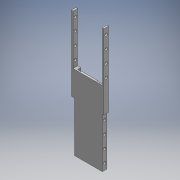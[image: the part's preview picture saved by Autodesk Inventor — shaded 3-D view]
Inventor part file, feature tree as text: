
AUTODESK INVENTOR PART (.ipt)
format: ipt  version: 2016 (Build 200138000, 138)  size: 206,336 bytes
history: native  units: mm
features: sketch x5, extrude x3, hole x2
ambient origin geometry x8: Origin, YZ Plane, XZ Plane, XY Plane, X Axis, Y Axis, Z Axis, Center Point
bodies: Solid1 (feature_tree)
feature tree (10):
  extrude  "Extrusion1"  Depth=80.0mm
  extrude  "Extrusion3"  Depth=2.5mm
  extrude  "Extrusion4"  Depth=44.5mm
  hole  "Hole1"  [1 undecoded]
  hole  "Hole2"  [1 undecoded]
  sketch  "Sketch1"  dims[d0=2.5mm d1=80.0mm]
  sketch  "Sketch4"  dims[d2=47.0mm d3=2.5mm]
  sketch  "Sketch5"  dims[d4=10.0mm d8=44.5mm]
  sketch  "Sketch6"  dims[d9=2.0mm d10=0.0mm d16=80.0mm]
  sketch  "Sketch7"  dims[d17=90.0deg d18=80.0mm d19=13.0mm d20=26.0mm d21=1.0mm d22=0.0mm d23=2.5mm d24=2.5mm d25=5.3mm d26=0.0mm d27=4.3mm d28=10.0mm d29=20.0mm d30=20.0mm d31=20.0mm d32=4.3mm d33=4.3mm d34=4.3mm d35=10.0mm d36=180.0deg d37=20.0mm d38=20.0mm d39=20.0mm d40=4.3mm d41=4.3mm d42=4.3mm d43=4.3mm d44=4.3mm d45=6.0mm d46=4.0mm d47=2.0mm d48=90.0deg d49=5.0mm d50=20.594885mm d51=4.3mm d52=4.3mm d53=4.3mm d54=4.3mm d55=4.3mm d56=4.3mm d57=4.3mm d58=4.3mm d59=4.3mm d60=6.0mm d61=4.0mm d62=2.0mm d63=90.0deg d64=5.0mm d65=20.594885mm d66=40.0mm]
note: 2 required parameter values undecoded (feature->parameter linkage not recoverable at this tier; creation-order binding heuristic only, values carry confidence <= 0.55)
